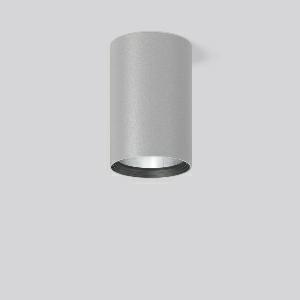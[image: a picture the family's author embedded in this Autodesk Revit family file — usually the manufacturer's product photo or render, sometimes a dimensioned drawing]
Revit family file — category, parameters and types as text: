
# Revit family: heledon_maxi_a_931246_004_2_76_0e37
name_source: partatom
category: Lighting Fixtures
units: mm (PartAtom-declared; Revit-internal decimal feet)

## family parameters
Cut with Voids When Loaded = No
Host = Face
Light Source = No
Part Type = Normal
Room Calculation Point = No
Round Connector Dimension = Use Diameter
Shared = No

## types (1)
- HELEDON maxi A (1 x LED Modul 927 bakery, 3450 lm, 2700)
    Apparent Load = 33 VA
    Approval mark = CE
    CIE Flux Codes = 100 100 100 100 100
    Color Rendering = 90
    Color Temperature = 2700
    Default Elevation = 1800 mm
    Description = Series: HELEDON maxi
Cylindrical surface-mounted downlight. Housing: die-cast aluminium, powder-coated. Internal ceiling frame polycarbonate with bayonet mounting. Black plastic ring and recessed LED to prevent glare from the side. Optical assembly with reflector made of MIRO-Silver with 98% total light reflection for outstanding efficiency - can be changed without tools. Special LED for illumination of pastries included. Suitable for Ceiling mounting. Easy installation with a separate ceiling frame with bayonet mounting and plug connection. Driver integrated. Connected via plug-in connector. High quality converter without flickering and stroboscopic effect. The following accessories can be mounted without use of tools: interchangeable lenses, decorative glasses, honeycomb louvre, clear and frosted diffusers, white interchangeable plastic ring. 
Colour: silver
Diameter: 123 mm
Height: 183 mm
Lamp: LED
Socket: without socket
Colour temperature: bakery
Colour rendering index (CRI): 97
System power: 33 W
Rated luminous flux: 3450 lm
Luminous efficiency: 105 lm/W
Control gear: Converter, dimmable, DALI
Protection class: I
Type of protection: IP 20
    Height = 183 mm
    Lamp = 1 x LED Modul 927 bakery
    Lamp Light Flux = 3450 lm
    Lamp count = 1
    Length = 123 mm
    Lifetime = 50000 h
    Luminous efficacy = 105 lm/W
    Manufacturer = RZB
    ModVariant = No
    Model = 931246.004.2.76
    Mounting Place = Ceiling
    Mounting Type = Surface mounted
    Number of Poles = 1
    OnlyDefault = Yes
    Power Factor = 1
    Product Name = HELEDON maxi A
    Product group = Surface mounted downlights
    ProductGroupID = 302
    Protection Class = Protection class I
    Protection Degree = IP 20
    RLX_Detail_Level = 1
    RLX_Emergency_Light_Flux = 0 lm
    RLX_Emergency_Type = 0
    RLX_Emergency_Type_DB = No
    RlxData = <blob elided: 99317 chars, md5=62be5ae3>
    Socket = socket
    Standby Power = 0 W
    System Light Flux = 3450 lm
    System Power = 33 W
    Type Comments = Product without accessories
    Type Image = 931192.004.jpg
    URL = http://relux.com
    VarID = ---
    Voltage = 230 V
    Voltage Range = 220-240 V
    Weight = 0.00 kg
    Width = 0 mm  [stored 0 ft]

note: [stored X ft] marks values corroborated as IEEE doubles in the binary element streams (Revit-internal decimal feet)

## geometry (parser evidence)
native form markers: Blend x4, Sweep x10
no freeform markers — native parametric forms only
